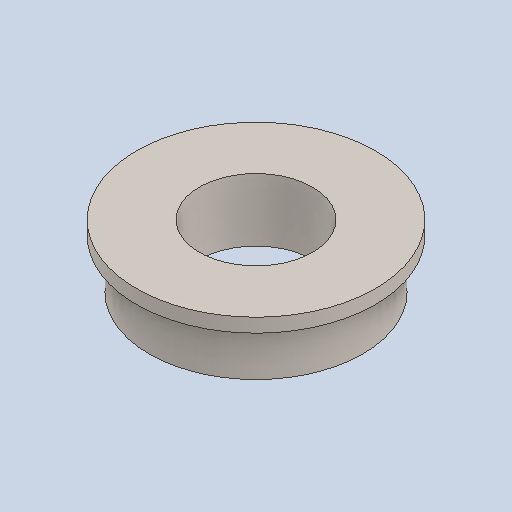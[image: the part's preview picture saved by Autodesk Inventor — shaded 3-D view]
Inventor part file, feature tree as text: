
AUTODESK INVENTOR PART (.ipt)
format: ipt  version: 2024.2 (Build 282272000, 272)  size: 105,472 bytes
history: native  units: in
note: dims shown in document units (in); Inventor stores cm internally (conversion verified against a paired STEP export)
features: revolve x1
ambient origin geometry x8: Origin, YZ Plane, XZ Plane, XY Plane, X Axis, Y Axis, Z Axis, Center Point
bodies: Solid1 (feature_tree)
feature tree (1):
  revolve  "Revolve1"  [1 undecoded]
note: 1 required parameter value undecoded (feature->parameter linkage not recoverable at this tier; creation-order binding heuristic only, values carry confidence <= 0.55)
